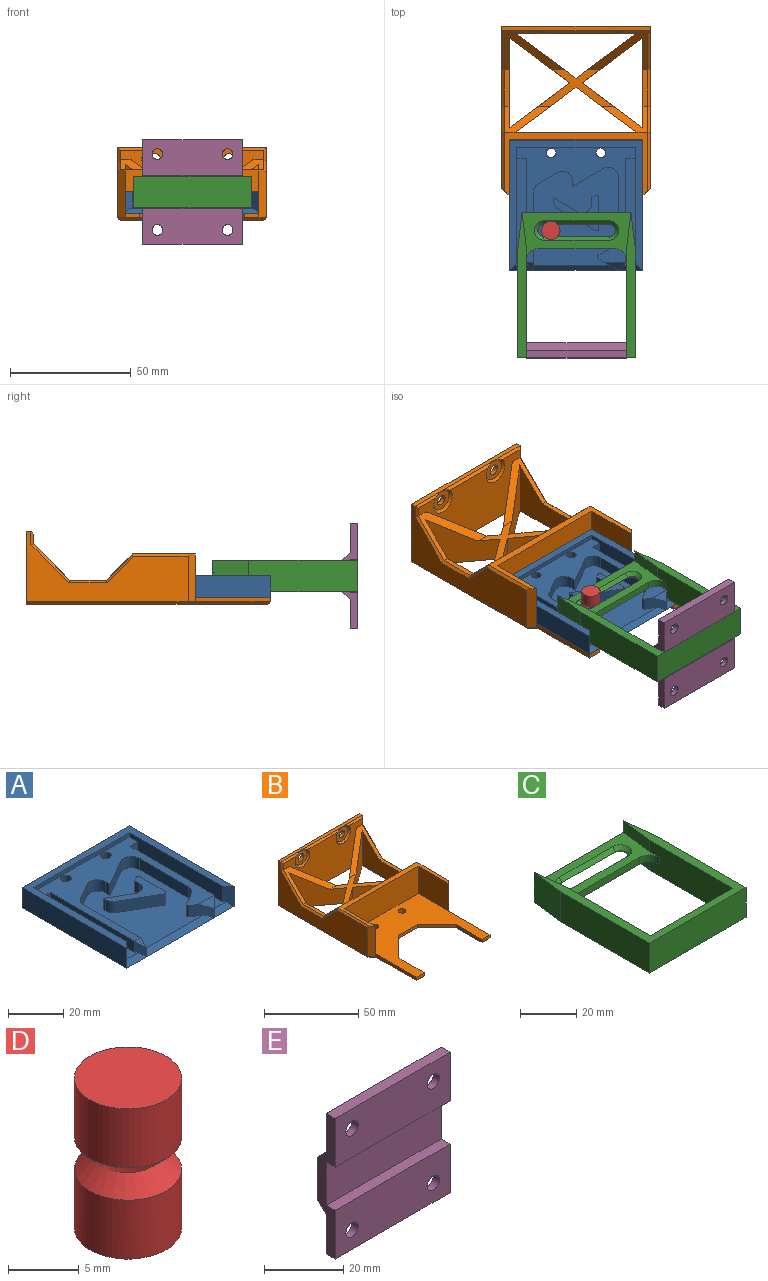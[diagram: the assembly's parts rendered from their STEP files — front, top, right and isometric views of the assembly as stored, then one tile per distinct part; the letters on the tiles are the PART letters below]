
ASSEMBLY  parts=5 mates=4
PART A: 50 faces, bbox 55x53.8x8.9 mm
  f0: plane 49x47.78mm, normal (0,0,1), area 750.9mm2, adj f3,f4,f5,f6,f7,f8,f9,f10
  f1: plane 55x8.9mm, normal (0,1,0), area 489.5mm2, adj f2,f21,f22,f38
  f2: plane 53.78x8.9mm, normal (-1,0,0), area 478.7mm2, adj f1,f22,f38,f47
  f3: plane 47.78x6.9mm, normal (1,0,0), area 307.7mm2, adj f0,f4,f36,f37,f38,f47
  f4: plane 5x4mm, normal (0,-1,0), area 20mm2, adj f0,f3,f5,f36
  f5: plane 43.38x5mm, normal (-1,0,0), area 216.9mm2, adj f0,f4,f36,f44
  f6: plane 32.33x7mm, normal (1,0,0), area 159.2mm2, adj f0,f7,f35,f39,f44,f45
  f7: cylinder r=4mm len=5mm, axis (0,0,-1), area 20.9mm2, adj f0,f6,f8,f35
  f8: plane 8x5mm, normal (0.5,-0.87,0), area 46.2mm2, adj f0,f7,f9,f35
  f9: cylinder r=4mm len=6mm, axis (0,0,-1), area 41.9mm2, adj f0,f8,f10,f35
  f10: plane 5x2.31mm, normal (-1,0,0), area 11.5mm2, adj f0,f9,f11,f35
  f11: plane 13x7.51mm, normal (0.5,-0.87,0), area 75.1mm2, adj f0,f10,f12,f35
  f12: cylinder r=4mm len=6mm, axis (0,0,-1), area 41.9mm2, adj f0,f11,f13,f35
  f13: plane 25.4x5mm, normal (-1,0,0), area 127mm2, adj f0,f12,f14,f35
  f14: cylinder r=4mm len=5mm, axis (0,0,-1), area 20.9mm2, adj f0,f13,f15,f35
  f15: plane 6x5mm, normal (-0.5,0.87,0), area 34.6mm2, adj f0,f14,f16,f35
  f16: cylinder r=1mm len=5mm, axis (0,0,-1), area 10.5mm2, adj f0,f15,f17,f35
  f17: plane 8x7mm, normal (-0.5,-0.87,0), area 41.2mm2, adj f0,f16,f35,f39,f42,f43
  f18: plane 43.38x5mm, normal (1,0,0), area 216.9mm2, adj f0,f19,f23,f42
  f19: plane 5x4mm, normal (0,-1,0), area 20mm2, adj f0,f18,f20,f23
  f20: plane 47.78x6.9mm, normal (-1,0,0), area 307.7mm2, adj f0,f19,f23,f37,f38,f46
  f21: plane 53.78x8.9mm, normal (1,0,0), area 478.7mm2, adj f1,f22,f38,f46
  f22: plane 55x53.78mm, normal (0,0,-1), area 2932.9mm2, adj f1,f2,f21,f39,f40,f41,f48,f49
  f23: plane 44.38x6mm, normal (0,0,1), area 178.5mm2, adj f18,f19,f20,f40,f42,f46
  f24: plane 19x14.7mm, normal (0,0,1), area 107.5mm2, adj f25,f26,f27,f28,f29,f30,f31,f32
  f25: cylinder r=4mm len=6mm, axis (0,0,-1), area 41.9mm2, adj f24,f26,f34,f35
  f26: plane 5x2.31mm, normal (-1,0,0), area 11.5mm2, adj f24,f25,f27,f35
  f27: plane 5x1.5mm, normal (-0.5,0.87,0), area 8.7mm2, adj f24,f26,f28,f35
  f28: cylinder r=1mm len=5mm, axis (0,0,-1), area 10.5mm2, adj f24,f27,f29,f35
  f29: plane 12.7x5mm, normal (1,0,0), area 63.5mm2, adj f24,f28,f30,f35
  f30: cylinder r=1mm len=5mm, axis (0,0,-1), area 10.5mm2, adj f24,f29,f31,f35
  f31: plane 15.5x8.95mm, normal (-0.5,-0.87,0), area 89.5mm2, adj f24,f30,f32,f35
  f32: cylinder r=4mm len=5mm, axis (0,0,-1), area 20.9mm2, adj f24,f31,f33,f35
  f33: plane 5x1.15mm, normal (-1,0,0), area 5.8mm2, adj f24,f32,f34,f35
  f34: plane 10x5.77mm, normal (0.5,0.87,0), area 57.7mm2, adj f24,f25,f33,f35
  f35: plane 40.68x35mm, normal (0,0,1), area 1141.5mm2, adj f6,f7,f8,f9,f10,f11,f12,f13
  f36: plane 44.38x6mm, normal (0,0,1), area 178.5mm2, adj f3,f4,f5,f41,f44,f47
  f37: plane 49x1.9mm, normal (0,-1,0), area 93.1mm2, adj f0,f3,f20,f38
  f38: plane 55x53.78mm, normal (0,0,1), area 460.7mm2, adj f1,f2,f3,f20,f21,f37,f46,f47
  f39: plane 35x2mm, normal (0,-0.71,0.71), area 94.1mm2, adj f6,f17,f22,f35
  f40: plane 10x2mm, normal (0,-0.71,0.71), area 22.6mm2, adj f22,f23,f42,f46
  f41: plane 10x2mm, normal (0,-0.71,0.71), area 22.6mm2, adj f22,f36,f44,f47
  f42: plane 7x3mm, normal (0.71,-0.71,0), area 17.7mm2, adj f17,f18,f23,f40,f43
  f43: plane 8.2x3mm, normal (0,-0.71,0.71), area 17.4mm2, adj f0,f17,f42
  f44: plane 7x3mm, normal (-0.71,-0.71,0), area 17.7mm2, adj f5,f6,f36,f41,f45
  f45: plane 3x3mm, normal (0,-0.71,0.71), area 6.4mm2, adj f0,f6,f44
  f46: plane 8.9x3mm, normal (-0.71,-0.71,0), area 32.1mm2, adj f20,f21,f23,f38,f40
  f47: plane 8.9x3mm, normal (0.71,-0.71,0), area 32.1mm2, adj f2,f3,f36,f38,f41
  f48: cylinder r=2mm len=7mm, axis (0,0,-1), area 88mm2, adj f0,f22
  f49: cylinder r=2mm len=7mm, axis (0,0,-1), area 88mm2, adj f0,f22
PART B: 74 faces, bbox 61.4x101x30.9 mm
  f0: plane 31.26x15.2mm, normal (0,0,1), area 143.9mm2, adj f4,f6,f8,f9,f23,f24,f25,f27
  f1: plane 15.2x2mm, normal (0,0,1), area 30.4mm2, adj f7,f36,f39,f49
  f2: plane 50.36x19.8mm, normal (0,1,0), area 997.1mm2, adj f6,f23,f33,f65
  f3: plane 59.4x28mm, normal (0,-1,0), area 1279.3mm2, adj f9,f25,f36,f37,f44,f45,f46,f64
  f4: plane 25.18x23.13mm, normal (0.59,-0.8,0), area 458.2mm2, adj f0,f5,f27,f29,f37
  f5: plane 37.27x23.13mm, normal (-1,0,0), area 498.8mm2, adj f4,f27,f29,f35,f37,f38
  f6: plane 26.53x20.8mm, normal (0.59,-0.8,0), area 412.1mm2, adj f0,f2,f23,f29,f39,f65
  f7: plane 37.27x23.13mm, normal (1,0,0), area 498.8mm2, adj f1,f8,f24,f29,f36,f39
  f8: plane 25.18x23.13mm, normal (-0.59,-0.8,0), area 458.2mm2, adj f0,f7,f24,f29,f36
  f9: plane 26.53x25mm, normal (0.59,0.8,0), area 503.2mm2, adj f0,f3,f25,f29,f36,f64
  f10: plane 67x29mm, normal (1,0,0), area 1001.7mm2, adj f11,f26,f34,f40,f41,f42,f43,f44
  f11: plane 61.4x30mm, normal (0,1,0), area 1810.6mm2, adj f10,f12,f29,f34,f51,f61,f66,f68
  f12: plane 67x29mm, normal (-1,0,0), area 1001.7mm2, adj f11,f13,f34,f46,f47,f48,f49,f50
  f13: plane 19.8x3mm, normal (-0.71,-0.71,0), area 83.3mm2, adj f12,f14,f30,f33,f48,f52
  f14: plane 30.98x2mm, normal (-1,0,0), area 62mm2, adj f13,f15,f28,f53
  f15: plane 6x2mm, normal (0,-1,0), area 12mm2, adj f14,f16,f28,f54
  f16: plane 19.52x2mm, normal (1,0,0), area 39mm2, adj f15,f17,f28,f55
  f17: plane 14.47x14.47mm, normal (0.71,-0.71,0), area 40.9mm2, adj f16,f18,f28,f56
  f18: plane 14.47x2mm, normal (0,-1,0), area 28.9mm2, adj f17,f19,f28,f57
  f19: plane 14.47x14.47mm, normal (-0.71,-0.71,0), area 40.9mm2, adj f18,f20,f28,f58
  f20: plane 19.52x2mm, normal (-1,0,0), area 39mm2, adj f19,f21,f28,f59
  f21: plane 6x2mm, normal (0,-1,0), area 12mm2, adj f20,f22,f28,f60
  f22: plane 30.98x2mm, normal (1,0,0), area 62mm2, adj f21,f26,f28,f62
  f23: plane 26.53x20.8mm, normal (-0.59,-0.8,0), area 412.1mm2, adj f0,f2,f6,f29,f38,f65
  f24: plane 25.18x18.93mm, normal (-0.59,0.8,0), area 380.3mm2, adj f0,f7,f8,f29,f39
  f25: plane 26.53x25mm, normal (-0.59,0.8,0), area 503.2mm2, adj f0,f3,f9,f29,f37,f64
  f26: plane 19.8x3mm, normal (0.71,-0.71,0), area 83.3mm2, adj f10,f22,f32,f33,f40,f63
  f27: plane 25.18x18.93mm, normal (0.59,0.8,0), area 380.3mm2, adj f0,f4,f5,f29,f38
  f28: plane 55.4x53.98mm, normal (0,0,1), area 1699.9mm2, adj f14,f15,f16,f17,f18,f19,f20,f21
  f29: plane 99.98x59.4mm, normal (0,0,-1), area 2426.1mm2, adj f4,f5,f6,f7,f8,f9,f11,f23
  f30: plane 23x17.8mm, normal (1,0,0), area 409.4mm2, adj f13,f28,f31,f33
  f31: plane 55.4x17.8mm, normal (0,-1,0), area 986.1mm2, adj f28,f30,f32,f33
  f32: plane 23x17.8mm, normal (-1,0,0), area 409.4mm2, adj f26,f28,f31,f33
  f33: plane 59.4x26mm, normal (0,0,1), area 266.2mm2, adj f2,f13,f26,f30,f31,f32,f38,f39
  f34: plane 61.4x2mm, normal (0,0,1), area 122.8mm2, adj f10,f11,f12,f45
  f35: plane 15.2x2mm, normal (0,0,1), area 30.4mm2, adj f5,f37,f38,f42
  f36: plane 24.79x15mm, normal (0,-0.71,0.71), area 146.1mm2, adj f0,f1,f3,f7,f8,f9,f47
  f37: plane 24.79x15mm, normal (0,-0.71,0.71), area 146.1mm2, adj f0,f3,f4,f5,f25,f35,f43
  f38: plane 19.11x10.8mm, normal (0,0.71,0.71), area 104.2mm2, adj f0,f5,f23,f27,f33,f35,f41
  f39: plane 19.11x10.8mm, normal (0,0.71,0.71), area 104.2mm2, adj f0,f1,f6,f7,f24,f33,f50
  f40: plane 24x1mm, normal (0.71,0,0.71), area 32.9mm2, adj f10,f26,f33,f41
  f41: plane 11.8x11.21mm, normal (0.71,0.5,0.5), area 21.6mm2, adj f10,f38,f40,f42
  f42: plane 16.03x1mm, normal (0.71,0,0.71), area 22.1mm2, adj f10,f35,f41,f43
  f43: plane 16x16mm, normal (0.71,-0.5,0.5), area 30.6mm2, adj f10,f37,f42,f44
  f44: plane 5.41x1mm, normal (0.71,-0.71,0), area 6.7mm2, adj f3,f10,f43,f45
  f45: plane 61.4x1mm, normal (0,-0.71,0.71), area 70.8mm2, adj f3,f34,f44,f46,f72,f73
  f46: plane 5.41x1mm, normal (-0.71,-0.71,0), area 6.7mm2, adj f3,f12,f45,f47
  f47: plane 16x16mm, normal (-0.71,-0.5,0.5), area 30.6mm2, adj f12,f36,f46,f49
  f48: plane 24x1mm, normal (-0.71,0,0.71), area 32.9mm2, adj f12,f13,f33,f50
  f49: plane 16.03x1mm, normal (-0.71,0,0.71), area 22.1mm2, adj f1,f12,f47,f50
  f50: plane 11.8x11.21mm, normal (-0.71,0.5,0.5), area 21.6mm2, adj f12,f39,f48,f49
  f51: plane 67x1mm, normal (-0.71,0,-0.71), area 94.5mm2, adj f11,f12,f29,f52
  f52: plane 4x3.41mm, normal (-0.5,-0.5,-0.71), area 6mm2, adj f13,f29,f51,f53
  f53: plane 31.4x1mm, normal (-0.71,0,-0.71), area 43.4mm2, adj f14,f29,f52,f54
  f54: plane 6x1mm, normal (0,-0.71,-0.71), area 7.1mm2, adj f15,f29,f53,f55
  f55: plane 19.93x1mm, normal (0.71,0,-0.71), area 27.2mm2, adj f16,f29,f54,f56
  f56: plane 15.47x15.47mm, normal (0.5,-0.5,-0.71), area 29.5mm2, adj f17,f29,f55,f57
  f57: plane 15.3x1mm, normal (0,-0.71,-0.71), area 21mm2, adj f18,f29,f56,f58
  f58: plane 15.47x15.47mm, normal (-0.5,-0.5,-0.71), area 29.5mm2, adj f19,f29,f57,f59
  f59: plane 19.93x1mm, normal (-0.71,0,-0.71), area 27.2mm2, adj f20,f29,f58,f60
  f60: plane 6x1mm, normal (0,-0.71,-0.71), area 7.1mm2, adj f21,f29,f59,f62
  f61: plane 67x1mm, normal (0.71,0,-0.71), area 94.5mm2, adj f10,f11,f29,f63
  f62: plane 31.4x1mm, normal (0.71,0,-0.71), area 43.4mm2, adj f22,f29,f60,f63
  f63: plane 4x3.41mm, normal (0.5,-0.5,-0.71), area 6mm2, adj f26,f29,f61,f62
  f64: plane 53.06x1mm, normal (0,-0.71,-0.71), area 73.1mm2, adj f3,f9,f25,f29
  f65: plane 53.06x1mm, normal (0,0.71,-0.71), area 73.1mm2, adj f2,f6,f23,f29
  f66: cylinder r=2.2mm len=4.4mm, axis (0,-1,0), area 27.6mm2, adj f11,f67
  f67: plane 8.95x8.95mm, normal (0,-1,0), area 47.7mm2, adj f66,f72
  f68: cylinder r=2.2mm len=4.4mm, axis (0,-1,0), area 27.6mm2, adj f11,f69
  f69: plane 8.95x8.95mm, normal (0,-1,0), area 47.7mm2, adj f68,f73
  f70: cylinder r=2mm len=4mm, axis (0,0,-1), area 37.7mm2, adj f28,f29
  f71: cylinder r=2mm len=4mm, axis (0,0,-1), area 37.7mm2, adj f28,f29
  f72: cone r=4.47mm half-angle=45deg, axis (0,-1,0), area 36.3mm2, adj f3,f45,f67
  f73: cone r=4.47mm half-angle=45deg, axis (0,-1,0), area 36.3mm2, adj f3,f45,f69
PART C: 28 faces, bbox 48.6x60x13 mm
  f0: plane 31.4x3mm, normal (0,-1,0), area 94.2mm2, adj f1,f2,f26,f27
  f1: plane 45x20mm, normal (0,0,1), area 392.5mm2, adj f0,f3,f11,f12,f14,f15,f18,f19
  f2: plane 45x20mm, normal (0,0,-1), area 392.5mm2, adj f0,f3,f6,f7,f12,f14,f21,f22
  f3: plane 45x3mm, normal (0,1,0), area 135mm2, adj f1,f2,f4,f5
  f4: plane 15x13mm, normal (-0.99,0.12,0), area 196.4mm2, adj f3,f7,f8,f15,f16,f17
  f5: plane 15x13mm, normal (0.99,0.12,0), area 196.4mm2, adj f3,f6,f10,f11,f16,f17
  f6: plane 15x5mm, normal (-0.99,0.12,0), area 75.5mm2, adj f2,f5,f12,f17
  f7: plane 15x5mm, normal (0.99,0.12,0), area 75.5mm2, adj f2,f4,f14,f17
  f8: plane 45x13mm, normal (-1,0,0), area 585mm2, adj f4,f9,f16,f17
  f9: plane 48.6x13mm, normal (0,-1,0), area 631.8mm2, adj f8,f10,f16,f17
  f10: plane 45x13mm, normal (1,0,0), area 585mm2, adj f5,f9,f16,f17
  f11: plane 15x5mm, normal (-0.99,0.12,0), area 75.5mm2, adj f1,f5,f12,f16
  f12: plane 42x13mm, normal (-1,0,0), area 531mm2, adj f1,f2,f6,f11,f13,f16,f17,f26
  f13: plane 41.4x13mm, normal (0,1,0), area 538.2mm2, adj f12,f14,f16,f17
  f14: plane 42x13mm, normal (1,0,0), area 531mm2, adj f1,f2,f7,f13,f15,f16,f17,f27
  f15: plane 15x5mm, normal (0.99,0.12,0), area 75.5mm2, adj f1,f4,f14,f16
  f16: plane 60x48.6mm, normal (0,0,1), area 502.2mm2, adj f4,f5,f8,f9,f10,f11,f12,f13
  f17: plane 60x48.6mm, normal (0,0,-1), area 502.2mm2, adj f4,f5,f6,f7,f8,f9,f10,f12
  f18: cone r=2.5mm half-angle=45deg, axis (0,0,1), area 21.7mm2, adj f1,f19,f20,f21
  f19: plane 27x1.5mm, normal (0,-0.71,0.71), area 57.3mm2, adj f1,f18,f22,f23
  f20: plane 27x1.5mm, normal (0,0.71,0.71), area 57.3mm2, adj f1,f18,f23,f24
  f21: cone r=4mm half-angle=45deg, axis (0,0,-1), area 21.7mm2, adj f2,f18,f22,f24
  f22: plane 27x1.5mm, normal (0,-0.71,-0.71), area 57.3mm2, adj f2,f19,f21,f25
  f23: cone r=4mm half-angle=45deg, axis (0,0,1), area 21.7mm2, adj f1,f19,f20,f25
  f24: plane 27x1.5mm, normal (0,0.71,-0.71), area 57.3mm2, adj f2,f20,f21,f25
  f25: cone r=2.5mm half-angle=45deg, axis (0,0,-1), area 21.7mm2, adj f2,f22,f23,f24
  f26: cylinder r=5mm len=5mm, axis (0,0,-1), area 23.6mm2, adj f0,f1,f2,f12
  f27: cylinder r=5mm len=5mm, axis (0,0,1), area 23.6mm2, adj f0,f1,f2,f14
PART D: 6 faces, bbox 7.6x7.6x13 mm
  f0: cylinder r=3.8mm len=7.6mm, axis (0,0,-1), area 121.8mm2, adj f1,f4
  f1: plane 7.6x7.6mm, normal (0,0,-1), area 45.4mm2, adj f0
  f2: cylinder r=3.8mm len=7.6mm, axis (0,0,-1), area 121.8mm2, adj f3,f5
  f3: plane 7.6x7.6mm, normal (0,0,1), area 45.4mm2, adj f2
  f4: cone r=3.9mm half-angle=45deg, axis (0,0,-1), area 38.6mm2, adj f0,f5
  f5: cone r=3.9mm half-angle=45deg, axis (0,0,1), area 38.6mm2, adj f2,f4
PART E: 26 faces, bbox 41x6.2x43.4 mm
  f0: plane 41x15mm, normal (0,-1,0), area 584.6mm2, adj f1,f11,f12,f13,f14,f16
  f1: plane 41x3.2mm, normal (0,0,-1), area 131.2mm2, adj f0,f2,f12,f13
  f2: plane 41x13.4mm, normal (0,-1,0), area 549.4mm2, adj f1,f3,f12,f13
  f3: plane 41x3.2mm, normal (0,0,1), area 131.2mm2, adj f2,f4,f12,f13
  f4: plane 41x15mm, normal (0,-1,0), area 584.6mm2, adj f3,f5,f12,f13,f18,f20
  f5: plane 41x3.2mm, normal (0,0,-1), area 131.2mm2, adj f4,f6,f12,f13
  f6: plane 41x12mm, normal (0,1,0), area 303.7mm2, adj f5,f7,f12,f13,f22,f23
  f7: plane 41x3mm, normal (0,0.71,-0.71), area 173.9mm2, adj f6,f8,f12,f13
  f8: plane 41x13.4mm, normal (0,1,0), area 549.4mm2, adj f7,f9,f12,f13
  f9: plane 41x3mm, normal (0,0.71,0.71), area 173.9mm2, adj f8,f10,f12,f13
  f10: plane 41x12mm, normal (0,1,0), area 303.7mm2, adj f9,f11,f12,f13,f24,f25
  f11: plane 41x3.2mm, normal (0,0,1), area 131.2mm2, adj f0,f10,f12,f13
  f12: plane 43.4x6.2mm, normal (1,0,0), area 145.2mm2, adj f0,f1,f2,f3,f4,f5,f6,f7
  f13: plane 43.4x6.2mm, normal (-1,0,0), area 145.2mm2, adj f0,f1,f2,f3,f4,f5,f6,f7
  f14: cylinder r=2.2mm len=4.4mm, axis (0,1,0), area 30.4mm2, adj f0,f15
  f15: plane 8.95x8.95mm, normal (0,1,0), area 47.7mm2, adj f14,f24
  f16: cylinder r=2.2mm len=4.4mm, axis (0,1,0), area 30.4mm2, adj f0,f17
  f17: plane 8.95x8.95mm, normal (0,1,0), area 47.7mm2, adj f16,f25
  f18: cylinder r=2.2mm len=4.4mm, axis (0,1,0), area 30.4mm2, adj f4,f19
  f19: plane 8.95x8.95mm, normal (0,1,0), area 47.7mm2, adj f18,f22
  f20: cylinder r=2.2mm len=4.4mm, axis (0,1,0), area 30.4mm2, adj f4,f21
  f21: plane 8.95x8.95mm, normal (0,1,0), area 47.7mm2, adj f20,f23
  f22: cone r=4.47mm half-angle=45deg, axis (0,1,0), area 44.2mm2, adj f6,f19
  f23: cone r=4.47mm half-angle=45deg, axis (0,1,0), area 44.2mm2, adj f6,f21
  f24: cone r=4.47mm half-angle=45deg, axis (0,1,0), area 44.2mm2, adj f10,f15
  f25: cone r=4.47mm half-angle=45deg, axis (0,1,0), area 44.2mm2, adj f10,f17
PLACE A t=(-0.92,-24.33,0.03)mm fixed
PLACE B t=(-0.92,-24.33,-2.97)mm
PLACE C rot(axis=(0,-1,0),180deg) t=(-19.7,-7.91,10.23)mm
PLACE D rot(axis=(0,0,1),27.4deg) t=(-20.81,-7.91,2.23)mm
PLACE E rot(axis=(0.06,-0.02,1),0deg) t=(-10.2,-8.11,7.23)mm
MATE fastened A.f49 <-> B.f71  axis (0,0,-1) through (-20.67,24.25,0.03)mm
MATE pin_slot D.f4 <-> C.f18  axis (0,0,1) through (-20.81,-7.91,8.73)mm
MATE planar A.f35 <-> D.f0  axis (0,0,1) through (-10.84,-3.37,2.03)mm
MATE fastened C.f13 <-> E.f2  axis (0,1,0) through (-10.2,-57.41,8.73)mm
